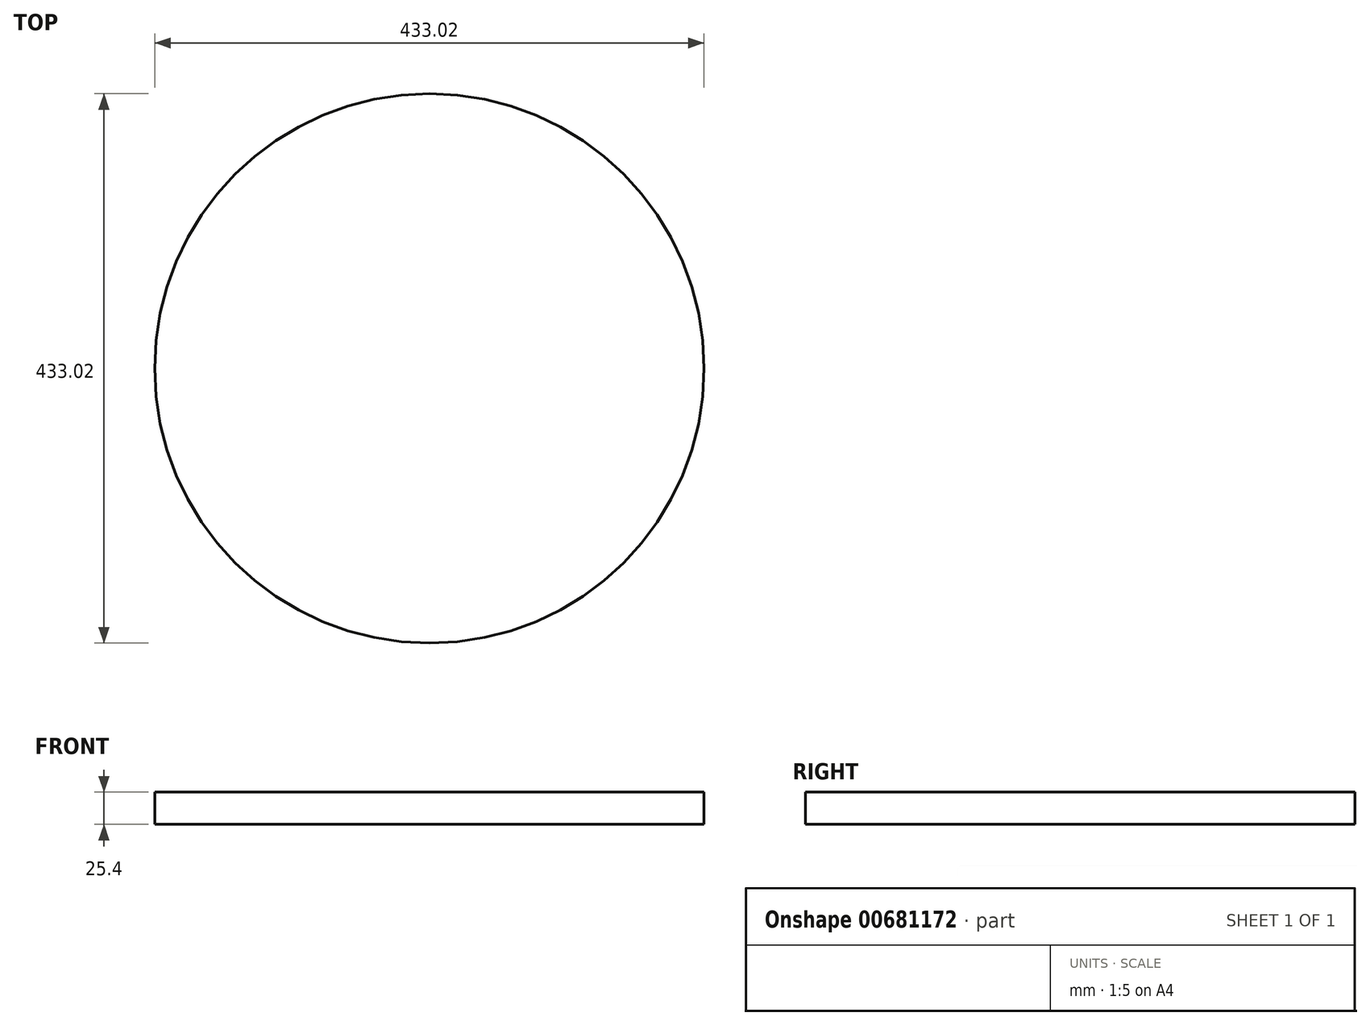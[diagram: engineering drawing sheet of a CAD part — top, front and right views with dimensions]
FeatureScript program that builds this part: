
annotation { "Feature Type Name" : "Feature", "Feature Type Description" : "" }
export const myFeature = defineFeature(function(context is Context, id is Id, definition is map)
    precondition{}
    {
        {
            var Q0;
            Q0=qCreatedBy(makeId("Top.planeOp"),FACE);
            var sketch = newSketch(context, id + "F0", { "sketchPlane" : qUnion([Q0])});
            skCircle(sketch, "E0", {"center": v(-201.68, 491.9) * mm, "radius": 216.51 * mm});
            skSolve(sketch);
        }
        {
            var Q0;
            Q0 = qSketchRegion(id + "F0", true);
            extrude(context, id + "F1", {"entities" : qUnion([Q0]), "depth" : 25.4 * mm, "offsetDistance" : 25.4 * mm});
        }
    });
